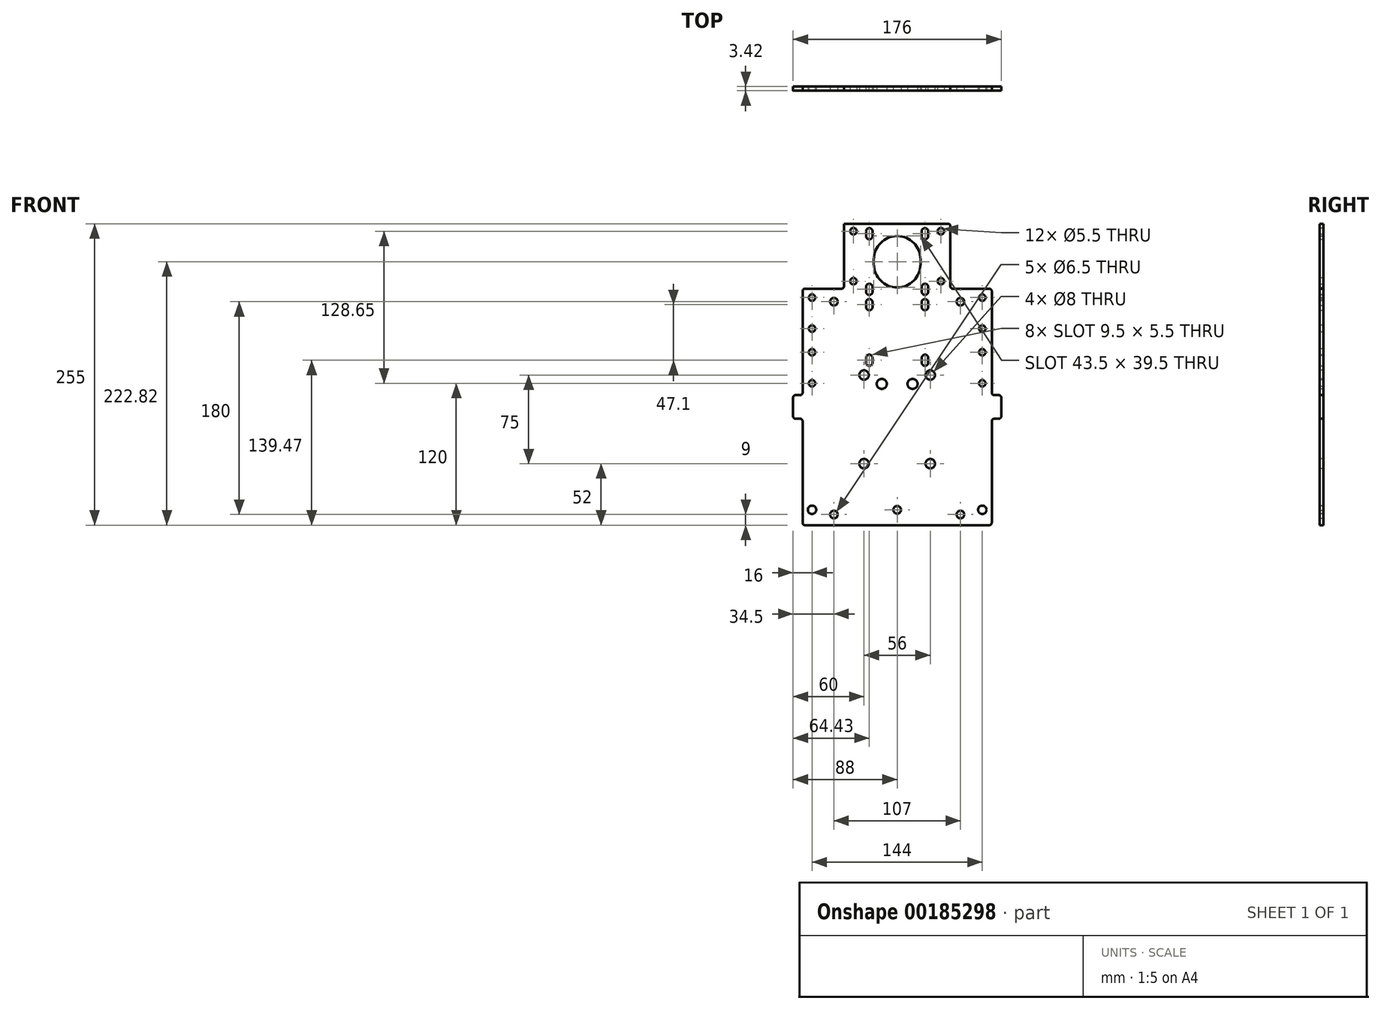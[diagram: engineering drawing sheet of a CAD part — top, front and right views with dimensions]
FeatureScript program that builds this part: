
annotation { "Feature Type Name" : "Feature", "Feature Type Description" : "" }
export const myFeature = defineFeature(function(context is Context, id is Id, definition is map)
    precondition{}
    {
        {
            var Q0;
            Q0=qCreatedBy(makeId("Front.planeOp"),FACE);
            var sketch = newSketch(context, id + "F0", { "sketchPlane" : qUnion([Q0])});
            skLineSegment(sketch, "E0", {"start": v(-80, -100) * mm, "end": v(80, -100) * mm});
            skLineSegment(sketch, "E1", {"start": v(80, -100) * mm, "end": v(80, -10) * mm});
            skLineSegment(sketch, "E2", {"start": v(80, -10) * mm, "end": v(88, -10) * mm});
            skLineSegment(sketch, "E3", {"start": v(88, -10) * mm, "end": v(88, 10) * mm});
            skLineSegment(sketch, "E4", {"start": v(88, 10) * mm, "end": v(80, 10) * mm});
            skLineSegment(sketch, "E5", {"start": v(80, 10) * mm, "end": v(80, 100) * mm});
            skLineSegment(sketch, "E6", {"start": v(80, 100) * mm, "end": v(45, 100) * mm});
            skLineSegment(sketch, "E7", {"start": v(45, 100) * mm, "end": v(45, 155) * mm});
            skLineSegment(sketch, "E8", {"start": v(45, 155) * mm, "end": v(-45, 155) * mm});
            skLineSegment(sketch, "E9", {"start": v(-45, 155) * mm, "end": v(-45, 100) * mm});
            skLineSegment(sketch, "E10", {"start": v(-45, 100) * mm, "end": v(-80, 100) * mm});
            skLineSegment(sketch, "E11", {"start": v(-80, 100) * mm, "end": v(-80, 10) * mm});
            skLineSegment(sketch, "E12", {"start": v(-80, 10) * mm, "end": v(-88, 10) * mm});
            skLineSegment(sketch, "E13", {"start": v(-88, 10) * mm, "end": v(-88, -10) * mm});
            skLineSegment(sketch, "E14", {"start": v(-88, -10) * mm, "end": v(-80, -10) * mm});
            skLineSegment(sketch, "E15", {"start": v(-80, -10) * mm, "end": v(-80, -100) * mm});
            skLineSegment(sketch, "E16", {"start": v(0, 155) * mm, "end": v(0, 0) * mm, "construction": true});
            skLineSegment(sketch, "E17", {"start": v(0, 0) * mm, "end": v(88, 0) * mm, "construction": true});
            skLineSegment(sketch, "E18", {"start": v(-19.75, 124.82) * mm, "end": v(-19.75, 120.82) * mm});
            skLineSegment(sketch, "E19", {"start": v(19.75, 124.82) * mm, "end": v(19.75, 120.82) * mm});
            skLineSegment(sketch, "E20", {"start": v(-19.75, 122.82) * mm, "end": v(19.75, 122.82) * mm, "construction": true});
            skPoint(sketch, "E21", {"position": v(0, 122.82) * mm});
            skArc(sketch, "E22", {"start": v(-19.75, 124.82) * mm, "mid": v(0, 144.57) * mm, "end": v(19.75, 124.82) * mm});
            skArc(sketch, "E23", {"start": v(-19.75, 120.82) * mm, "mid": v(0, 101.07) * mm, "end": v(19.75, 120.82) * mm});
            skLineSegment(sketch, "E24.bottom", {"start": v(-23.57, 146.57) * mm, "end": v(23.53, 146.57) * mm, "construction": true});
            skLineSegment(sketch, "E24.top", {"start": v(-23.57, 99.47) * mm, "end": v(23.53, 99.47) * mm, "construction": true});
            skLineSegment(sketch, "E24.left", {"start": v(-23.57, 146.57) * mm, "end": v(-23.57, 99.47) * mm, "construction": true});
            skLineSegment(sketch, "E24.right", {"start": v(23.53, 146.57) * mm, "end": v(23.53, 99.47) * mm, "construction": true});
            skLineSegment(sketch, "E25.bottom", {"start": v(-20.82, 148.57) * mm, "end": v(-26.32, 148.57) * mm, "construction": true});
            skLineSegment(sketch, "E25.top", {"start": v(-20.82, 144.57) * mm, "end": v(-26.32, 144.57) * mm, "construction": true});
            skLineSegment(sketch, "E25.left", {"start": v(-20.82, 148.57) * mm, "end": v(-20.82, 144.57) * mm});
            skLineSegment(sketch, "E25.right", {"start": v(-26.32, 148.57) * mm, "end": v(-26.32, 144.57) * mm});
            skPoint(sketch, "E25.middle", {"position": v(-23.57, 146.57) * mm});
            skLineSegment(sketch, "E26.bottom", {"start": v(26.28, 148.57) * mm, "end": v(20.78, 148.57) * mm, "construction": true});
            skLineSegment(sketch, "E26.top", {"start": v(26.28, 144.57) * mm, "end": v(20.78, 144.57) * mm, "construction": true});
            skLineSegment(sketch, "E26.left", {"start": v(26.28, 148.57) * mm, "end": v(26.28, 144.57) * mm});
            skLineSegment(sketch, "E26.right", {"start": v(20.78, 148.57) * mm, "end": v(20.78, 144.57) * mm});
            skPoint(sketch, "E26.middle", {"position": v(23.53, 146.57) * mm});
            skLineSegment(sketch, "E27.bottom", {"start": v(26.28, 101.47) * mm, "end": v(20.78, 101.47) * mm, "construction": true});
            skLineSegment(sketch, "E27.top", {"start": v(26.28, 97.47) * mm, "end": v(20.78, 97.47) * mm, "construction": true});
            skLineSegment(sketch, "E27.left", {"start": v(26.28, 101.47) * mm, "end": v(26.28, 97.47) * mm});
            skLineSegment(sketch, "E27.right", {"start": v(20.78, 101.47) * mm, "end": v(20.78, 97.47) * mm});
            skPoint(sketch, "E27.middle", {"position": v(23.53, 99.47) * mm});
            skLineSegment(sketch, "E28.bottom", {"start": v(-20.82, 101.47) * mm, "end": v(-26.32, 101.47) * mm, "construction": true});
            skLineSegment(sketch, "E28.top", {"start": v(-20.82, 97.47) * mm, "end": v(-26.32, 97.47) * mm, "construction": true});
            skLineSegment(sketch, "E28.left", {"start": v(-20.82, 101.47) * mm, "end": v(-20.82, 97.47) * mm});
            skLineSegment(sketch, "E28.right", {"start": v(-26.32, 101.47) * mm, "end": v(-26.32, 97.47) * mm});
            skPoint(sketch, "E28.middle", {"position": v(-23.57, 99.47) * mm});
            skLineSegment(sketch, "E29.bottom", {"start": v(-23.57, 86.57) * mm, "end": v(23.53, 86.57) * mm, "construction": true});
            skLineSegment(sketch, "E29.top", {"start": v(-23.57, 39.47) * mm, "end": v(23.53, 39.47) * mm, "construction": true});
            skLineSegment(sketch, "E29.left", {"start": v(-23.57, 86.57) * mm, "end": v(-23.57, 39.47) * mm, "construction": true});
            skLineSegment(sketch, "E29.right", {"start": v(23.53, 86.57) * mm, "end": v(23.53, 39.47) * mm, "construction": true});
            skLineSegment(sketch, "E30.bottom", {"start": v(-20.82, 88.57) * mm, "end": v(-26.32, 88.57) * mm, "construction": true});
            skLineSegment(sketch, "E30.top", {"start": v(-20.82, 84.57) * mm, "end": v(-26.32, 84.57) * mm, "construction": true});
            skLineSegment(sketch, "E30.left", {"start": v(-20.82, 88.57) * mm, "end": v(-20.82, 84.57) * mm});
            skLineSegment(sketch, "E30.right", {"start": v(-26.32, 88.57) * mm, "end": v(-26.32, 84.57) * mm});
            skPoint(sketch, "E30.middle", {"position": v(-23.57, 86.57) * mm});
            skLineSegment(sketch, "E31.bottom", {"start": v(26.28, 88.57) * mm, "end": v(20.78, 88.57) * mm, "construction": true});
            skLineSegment(sketch, "E31.top", {"start": v(26.28, 84.57) * mm, "end": v(20.78, 84.57) * mm, "construction": true});
            skLineSegment(sketch, "E31.left", {"start": v(26.28, 88.57) * mm, "end": v(26.28, 84.57) * mm});
            skLineSegment(sketch, "E31.right", {"start": v(20.78, 88.57) * mm, "end": v(20.78, 84.57) * mm});
            skPoint(sketch, "E31.middle", {"position": v(23.53, 86.57) * mm});
            skLineSegment(sketch, "E32.bottom", {"start": v(26.28, 41.47) * mm, "end": v(20.78, 41.47) * mm, "construction": true});
            skLineSegment(sketch, "E32.top", {"start": v(26.28, 37.47) * mm, "end": v(20.78, 37.47) * mm, "construction": true});
            skLineSegment(sketch, "E32.left", {"start": v(26.28, 41.47) * mm, "end": v(26.28, 37.47) * mm});
            skLineSegment(sketch, "E32.right", {"start": v(20.78, 41.47) * mm, "end": v(20.78, 37.47) * mm});
            skPoint(sketch, "E32.middle", {"position": v(23.53, 39.47) * mm});
            skLineSegment(sketch, "E33.bottom", {"start": v(-20.82, 41.47) * mm, "end": v(-26.32, 41.47) * mm, "construction": true});
            skLineSegment(sketch, "E33.top", {"start": v(-20.82, 37.47) * mm, "end": v(-26.32, 37.47) * mm, "construction": true});
            skLineSegment(sketch, "E33.left", {"start": v(-20.82, 41.47) * mm, "end": v(-20.82, 37.47) * mm});
            skLineSegment(sketch, "E33.right", {"start": v(-26.32, 41.47) * mm, "end": v(-26.32, 37.47) * mm});
            skPoint(sketch, "E33.middle", {"position": v(-23.57, 39.47) * mm});
            skArc(sketch, "E34", {"start": v(-26.32, 148.57) * mm, "mid": v(-23.57, 151.32) * mm, "end": v(-20.82, 148.57) * mm});
            skArc(sketch, "E35", {"start": v(26.28, 148.57) * mm, "mid": v(23.53, 151.32) * mm, "end": v(20.78, 148.57) * mm});
            skArc(sketch, "E36", {"start": v(20.78, 144.57) * mm, "mid": v(23.53, 141.82) * mm, "end": v(26.28, 144.57) * mm});
            skArc(sketch, "E37", {"start": v(-26.32, 144.57) * mm, "mid": v(-23.57, 141.82) * mm, "end": v(-20.82, 144.57) * mm});
            skArc(sketch, "E38", {"start": v(-20.82, 101.47) * mm, "mid": v(-23.57, 104.22) * mm, "end": v(-26.32, 101.47) * mm});
            skArc(sketch, "E39", {"start": v(-26.32, 97.47) * mm, "mid": v(-23.57, 94.72) * mm, "end": v(-20.82, 97.47) * mm});
            skArc(sketch, "E40", {"start": v(-20.82, 88.57) * mm, "mid": v(-23.57, 91.32) * mm, "end": v(-26.32, 88.57) * mm});
            skArc(sketch, "E41", {"start": v(-26.32, 84.57) * mm, "mid": v(-23.57, 81.82) * mm, "end": v(-20.82, 84.57) * mm});
            skArc(sketch, "E42", {"start": v(-20.82, 41.47) * mm, "mid": v(-23.57, 44.22) * mm, "end": v(-26.32, 41.47) * mm});
            skArc(sketch, "E43", {"start": v(-26.32, 37.47) * mm, "mid": v(-23.57, 34.72) * mm, "end": v(-20.82, 37.47) * mm});
            skArc(sketch, "E44", {"start": v(26.28, 41.47) * mm, "mid": v(23.53, 44.22) * mm, "end": v(20.78, 41.47) * mm});
            skArc(sketch, "E45", {"start": v(20.78, 37.47) * mm, "mid": v(23.53, 34.72) * mm, "end": v(26.28, 37.47) * mm});
            skArc(sketch, "E46", {"start": v(20.78, 84.57) * mm, "mid": v(23.53, 81.82) * mm, "end": v(26.28, 84.57) * mm});
            skArc(sketch, "E47", {"start": v(26.28, 88.57) * mm, "mid": v(23.53, 91.32) * mm, "end": v(20.78, 88.57) * mm});
            skArc(sketch, "E48", {"start": v(20.78, 97.47) * mm, "mid": v(23.53, 94.72) * mm, "end": v(26.28, 97.47) * mm});
            skArc(sketch, "E49", {"start": v(26.28, 101.47) * mm, "mid": v(23.53, 104.22) * mm, "end": v(20.78, 101.47) * mm});
            skSolve(sketch);
        }
        {
            var Q0;
            Q0 = qSketchRegion(id + "F0", true);
            extrude(context, id + "F1", {"entities" : qUnion([Q0]), "depth" : 3.42 * mm});
        }
        {
            var Q0;
            Q0=makeQuery(id+"F1.opExtrude","SWEPT_EDGE",EDGE,{"disambiguationData":[OSD([sQuery(id+"F0.wireOp",EDGE,"E7"),sQuery(id+"F0.wireOp",EDGE,"E8")])]});
            var Q1;
            Q1=makeQuery(id+"F1.opExtrude","SWEPT_EDGE",EDGE,{"disambiguationData":[OSD([sQuery(id+"F0.wireOp",EDGE,"E6"),sQuery(id+"F0.wireOp",EDGE,"E7")])]});
            var Q2;
            Q2=makeQuery(id+"F1.opExtrude","SWEPT_EDGE",EDGE,{"disambiguationData":[OSD([sQuery(id+"F0.wireOp",EDGE,"E5"),sQuery(id+"F0.wireOp",EDGE,"E6")])]});
            var Q3;
            Q3=makeQuery(id+"F1.opExtrude","SWEPT_EDGE",EDGE,{"disambiguationData":[OSD([sQuery(id+"F0.wireOp",EDGE,"E9"),sQuery(id+"F0.wireOp",EDGE,"E10")])]});
            var Q4;
            Q4=makeQuery(id+"F1.opExtrude","SWEPT_EDGE",EDGE,{"disambiguationData":[OSD([sQuery(id+"F0.wireOp",EDGE,"E10"),sQuery(id+"F0.wireOp",EDGE,"E11")])]});
            var Q5;
            Q5=makeQuery(id+"F1.opExtrude","SWEPT_EDGE",EDGE,{"disambiguationData":[OSD([sQuery(id+"F0.wireOp",EDGE,"E11"),sQuery(id+"F0.wireOp",EDGE,"E12")])]});
            var Q6;
            Q6=makeQuery(id+"F1.opExtrude","SWEPT_EDGE",EDGE,{"disambiguationData":[OSD([sQuery(id+"F0.wireOp",EDGE,"E12"),sQuery(id+"F0.wireOp",EDGE,"E13")])]});
            var Q7;
            Q7=makeQuery(id+"F1.opExtrude","SWEPT_EDGE",EDGE,{"disambiguationData":[OSD([sQuery(id+"F0.wireOp",EDGE,"E13"),sQuery(id+"F0.wireOp",EDGE,"E14")])]});
            var Q8;
            Q8=makeQuery(id+"F1.opExtrude","SWEPT_EDGE",EDGE,{"disambiguationData":[OSD([sQuery(id+"F0.wireOp",EDGE,"E14"),sQuery(id+"F0.wireOp",EDGE,"E15")])]});
            var Q9;
            Q9=makeQuery(id+"F1.opExtrude","SWEPT_EDGE",EDGE,{"disambiguationData":[OSD([sQuery(id+"F0.wireOp",EDGE,"E0"),sQuery(id+"F0.wireOp",EDGE,"E15")])]});
            var Q10;
            Q10=makeQuery(id+"F1.opExtrude","SWEPT_EDGE",EDGE,{"disambiguationData":[OSD([sQuery(id+"F0.wireOp",EDGE,"E0"),sQuery(id+"F0.wireOp",EDGE,"E1")])]});
            var Q11;
            Q11=makeQuery(id+"F1.opExtrude","SWEPT_EDGE",EDGE,{"disambiguationData":[OSD([sQuery(id+"F0.wireOp",EDGE,"E1"),sQuery(id+"F0.wireOp",EDGE,"E2")])]});
            var Q12;
            Q12=makeQuery(id+"F1.opExtrude","SWEPT_EDGE",EDGE,{"disambiguationData":[OSD([sQuery(id+"F0.wireOp",EDGE,"E2"),sQuery(id+"F0.wireOp",EDGE,"E3")])]});
            var Q13;
            Q13=makeQuery(id+"F1.opExtrude","SWEPT_EDGE",EDGE,{"disambiguationData":[OSD([sQuery(id+"F0.wireOp",EDGE,"E3"),sQuery(id+"F0.wireOp",EDGE,"E4")])]});
            var Q14;
            Q14=makeQuery(id+"F1.opExtrude","SWEPT_EDGE",EDGE,{"disambiguationData":[OSD([sQuery(id+"F0.wireOp",EDGE,"E4"),sQuery(id+"F0.wireOp",EDGE,"E5")])]});
            fillet(context, id + "F2", {"entities" : qUnion([Q0, Q1, Q2, Q3, Q4, Q5, Q6, Q7, Q8, Q9, Q10, Q11, Q12, Q13, Q14]), "radius" : 2 * mm, "tangentPropagation" : true, "allowEdgeOverflow" : false});
        }
        {
            var Q0;
            Q0=makeQuery(id+"F1.opExtrude","CAP_FACE",FACE,{"disambiguationData":[OSD([sQuery(id+"F0.wireOp",EDGE,"E0"),sQuery(id+"F0.wireOp",EDGE,"E1"),sQuery(id+"F0.wireOp",EDGE,"E2"),sQuery(id+"F0.wireOp",EDGE,"E3"),sQuery(id+"F0.wireOp",EDGE,"E4"),sQuery(id+"F0.wireOp",EDGE,"E5"),sQuery(id+"F0.wireOp",EDGE,"E6"),sQuery(id+"F0.wireOp",EDGE,"E7"),sQuery(id+"F0.wireOp",EDGE,"E8"),sQuery(id+"F0.wireOp",EDGE,"E9"),sQuery(id+"F0.wireOp",EDGE,"E10"),sQuery(id+"F0.wireOp",EDGE,"E11"),sQuery(id+"F0.wireOp",EDGE,"E12"),sQuery(id+"F0.wireOp",EDGE,"E13"),sQuery(id+"F0.wireOp",EDGE,"E14"),sQuery(id+"F0.wireOp",EDGE,"E15"),sQuery(id+"F0.wireOp",EDGE,"E18"),sQuery(id+"F0.wireOp",EDGE,"E19"),sQuery(id+"F0.wireOp",EDGE,"E22"),sQuery(id+"F0.wireOp",EDGE,"E23"),sQuery(id+"F0.wireOp",EDGE,"E25.left"),sQuery(id+"F0.wireOp",EDGE,"E25.right"),sQuery(id+"F0.wireOp",EDGE,"E26.left"),sQuery(id+"F0.wireOp",EDGE,"E26.right"),sQuery(id+"F0.wireOp",EDGE,"E27.left"),sQuery(id+"F0.wireOp",EDGE,"E27.right"),sQuery(id+"F0.wireOp",EDGE,"E28.left"),sQuery(id+"F0.wireOp",EDGE,"E28.right"),sQuery(id+"F0.wireOp",EDGE,"E30.left"),sQuery(id+"F0.wireOp",EDGE,"E30.right"),sQuery(id+"F0.wireOp",EDGE,"E31.left"),sQuery(id+"F0.wireOp",EDGE,"E31.right"),sQuery(id+"F0.wireOp",EDGE,"E32.left"),sQuery(id+"F0.wireOp",EDGE,"E32.right"),sQuery(id+"F0.wireOp",EDGE,"E33.left"),sQuery(id+"F0.wireOp",EDGE,"E33.right"),sQuery(id+"F0.wireOp",EDGE,"E34"),sQuery(id+"F0.wireOp",EDGE,"E35"),sQuery(id+"F0.wireOp",EDGE,"E36"),sQuery(id+"F0.wireOp",EDGE,"E37"),sQuery(id+"F0.wireOp",EDGE,"E38"),sQuery(id+"F0.wireOp",EDGE,"E39"),sQuery(id+"F0.wireOp",EDGE,"E40"),sQuery(id+"F0.wireOp",EDGE,"E41"),sQuery(id+"F0.wireOp",EDGE,"E42"),sQuery(id+"F0.wireOp",EDGE,"E43"),sQuery(id+"F0.wireOp",EDGE,"E44"),sQuery(id+"F0.wireOp",EDGE,"E45"),sQuery(id+"F0.wireOp",EDGE,"E46"),sQuery(id+"F0.wireOp",EDGE,"E47"),sQuery(id+"F0.wireOp",EDGE,"E48"),sQuery(id+"F0.wireOp",EDGE,"E49")])],"isStart":false});
            var sketch = newSketch(context, id + "F3", { "sketchPlane" : qUnion([Q0])});
            skLineSegment(sketch, "E50.bottom", {"start": v(-37, 148.65) * mm, "end": v(37, 148.65) * mm, "construction": true});
            skLineSegment(sketch, "E50.top", {"start": v(-37, 106.35) * mm, "end": v(37, 106.35) * mm, "construction": true});
            skLineSegment(sketch, "E50.left", {"start": v(-37, 148.65) * mm, "end": v(-37, 106.35) * mm, "construction": true});
            skLineSegment(sketch, "E50.right", {"start": v(37, 148.65) * mm, "end": v(37, 106.35) * mm, "construction": true});
            skLineSegment(sketch, "E51.bottom", {"start": v(-72, 92.5) * mm, "end": v(72, 92.5) * mm, "construction": true});
            skLineSegment(sketch, "E51.top", {"start": v(-72, 66.25) * mm, "end": v(72, 66.25) * mm, "construction": true});
            skLineSegment(sketch, "E51.left", {"start": v(-72, 92.5) * mm, "end": v(-72, 66.25) * mm, "construction": true});
            skLineSegment(sketch, "E51.right", {"start": v(72, 92.5) * mm, "end": v(72, 66.25) * mm, "construction": true});
            skLineSegment(sketch, "E52.bottom", {"start": v(-72, 46.25) * mm, "end": v(72, 46.25) * mm, "construction": true});
            skLineSegment(sketch, "E52.top", {"start": v(-72, 20) * mm, "end": v(72, 20) * mm, "construction": true});
            skLineSegment(sketch, "E52.left", {"start": v(-72, 46.25) * mm, "end": v(-72, 20) * mm, "construction": true});
            skLineSegment(sketch, "E52.right", {"start": v(72, 46.25) * mm, "end": v(72, 20) * mm, "construction": true});
            skLineSegment(sketch, "E53.bottom", {"start": v(-28, 27) * mm, "end": v(28, 27) * mm, "construction": true});
            skLineSegment(sketch, "E53.top", {"start": v(-28, -48) * mm, "end": v(28, -48) * mm, "construction": true});
            skLineSegment(sketch, "E53.left", {"start": v(-28, 27) * mm, "end": v(-28, -48) * mm, "construction": true});
            skLineSegment(sketch, "E53.right", {"start": v(28, 27) * mm, "end": v(28, -48) * mm, "construction": true});
            skLineSegment(sketch, "E54", {"start": v(-72, -87) * mm, "end": v(0, -87) * mm, "construction": true});
            skLineSegment(sketch, "E55", {"start": v(0, -87) * mm, "end": v(72, -87) * mm, "construction": true});
            skLineSegment(sketch, "E56", {"start": v(72, -87) * mm, "end": v(53.5, -91) * mm, "construction": true});
            skLineSegment(sketch, "E57", {"start": v(53.5, -91) * mm, "end": v(-53.5, -91) * mm, "construction": true});
            skLineSegment(sketch, "E58", {"start": v(-53.5, -91) * mm, "end": v(-72, -87) * mm, "construction": true});
            skLineSegment(sketch, "E59", {"start": v(-28, 19.5) * mm, "end": v(-13, 19.5) * mm, "construction": true});
            skLineSegment(sketch, "E60", {"start": v(-13, 19.5) * mm, "end": v(13, 19.5) * mm, "construction": true});
            skLineSegment(sketch, "E61", {"start": v(13, 19.5) * mm, "end": v(28, 19.5) * mm, "construction": true});
            skLineSegment(sketch, "E62", {"start": v(0, 19.5) * mm, "end": v(0, 0) * mm, "construction": true});
            skLineSegment(sketch, "E63", {"start": v(-53.5, -91) * mm, "end": v(-53.5, 89) * mm, "construction": true});
            skLineSegment(sketch, "E64", {"start": v(-53.5, 89) * mm, "end": v(53.5, 89) * mm, "construction": true});
            skLineSegment(sketch, "E65", {"start": v(53.5, 89) * mm, "end": v(53.5, -91) * mm, "construction": true});
            skSolve(sketch);
        }
        {
            var Q0;
            Q0=sQuery(id+"F3.wireOp",VERTEX,"E53.left.start");
            var Q1;
            Q1=sQuery(id+"F3.wireOp",VERTEX,"E53.right.start");
            var Q2;
            Q2=sQuery(id+"F3.wireOp",VERTEX,"E53.top.end");
            var Q3;
            Q3=sQuery(id+"F3.wireOp",VERTEX,"E53.top.start");
            var Q4;
            Q4=makeQuery(id+"F1.opExtrude","SWEPT_BODY",BODY,{"disambiguationData":[OSD([sQuery(id+"F0.wireOp",EDGE,"E0"),sQuery(id+"F0.wireOp",EDGE,"E1"),sQuery(id+"F0.wireOp",EDGE,"E2"),sQuery(id+"F0.wireOp",EDGE,"E3"),sQuery(id+"F0.wireOp",EDGE,"E4"),sQuery(id+"F0.wireOp",EDGE,"E5"),sQuery(id+"F0.wireOp",EDGE,"E6"),sQuery(id+"F0.wireOp",EDGE,"E7"),sQuery(id+"F0.wireOp",EDGE,"E8"),sQuery(id+"F0.wireOp",EDGE,"E9"),sQuery(id+"F0.wireOp",EDGE,"E10"),sQuery(id+"F0.wireOp",EDGE,"E11"),sQuery(id+"F0.wireOp",EDGE,"E12"),sQuery(id+"F0.wireOp",EDGE,"E13"),sQuery(id+"F0.wireOp",EDGE,"E14"),sQuery(id+"F0.wireOp",EDGE,"E15"),sQuery(id+"F0.wireOp",EDGE,"E18"),sQuery(id+"F0.wireOp",EDGE,"E19"),sQuery(id+"F0.wireOp",EDGE,"E22"),sQuery(id+"F0.wireOp",EDGE,"E23"),sQuery(id+"F0.wireOp",EDGE,"E25.left"),sQuery(id+"F0.wireOp",EDGE,"E25.right"),sQuery(id+"F0.wireOp",EDGE,"E26.left"),sQuery(id+"F0.wireOp",EDGE,"E26.right"),sQuery(id+"F0.wireOp",EDGE,"E27.left"),sQuery(id+"F0.wireOp",EDGE,"E27.right"),sQuery(id+"F0.wireOp",EDGE,"E28.left"),sQuery(id+"F0.wireOp",EDGE,"E28.right"),sQuery(id+"F0.wireOp",EDGE,"E30.left"),sQuery(id+"F0.wireOp",EDGE,"E30.right"),sQuery(id+"F0.wireOp",EDGE,"E31.left"),sQuery(id+"F0.wireOp",EDGE,"E31.right"),sQuery(id+"F0.wireOp",EDGE,"E32.left"),sQuery(id+"F0.wireOp",EDGE,"E32.right"),sQuery(id+"F0.wireOp",EDGE,"E33.left"),sQuery(id+"F0.wireOp",EDGE,"E33.right"),sQuery(id+"F0.wireOp",EDGE,"E34"),sQuery(id+"F0.wireOp",EDGE,"E35"),sQuery(id+"F0.wireOp",EDGE,"E36"),sQuery(id+"F0.wireOp",EDGE,"E37"),sQuery(id+"F0.wireOp",EDGE,"E38"),sQuery(id+"F0.wireOp",EDGE,"E39"),sQuery(id+"F0.wireOp",EDGE,"E40"),sQuery(id+"F0.wireOp",EDGE,"E41"),sQuery(id+"F0.wireOp",EDGE,"E42"),sQuery(id+"F0.wireOp",EDGE,"E43"),sQuery(id+"F0.wireOp",EDGE,"E44"),sQuery(id+"F0.wireOp",EDGE,"E45"),sQuery(id+"F0.wireOp",EDGE,"E46"),sQuery(id+"F0.wireOp",EDGE,"E47"),sQuery(id+"F0.wireOp",EDGE,"E48"),sQuery(id+"F0.wireOp",EDGE,"E49")])]});
            hole(context, id + "F4", {"style" : HoleStyle.SIMPLE, "endStyle" : HoleEndStyle.THROUGH, "holeDiameter" : 8 * mm, "locations" : qUnion([Q0, Q1, Q2, Q3]), "scope" : qUnion([Q4]), "isTappedThrough" : true});
        }
        {
            var Q0;
            Q0=sQuery(id+"F3.wireOp",VERTEX,"E60.start");
            var Q1;
            Q1=sQuery(id+"F3.wireOp",VERTEX,"E61.start");
            var Q2;
            Q2=makeQuery(id+"F1.opExtrude","SWEPT_BODY",BODY,{"disambiguationData":[OSD([sQuery(id+"F0.wireOp",EDGE,"E0"),sQuery(id+"F0.wireOp",EDGE,"E1"),sQuery(id+"F0.wireOp",EDGE,"E2"),sQuery(id+"F0.wireOp",EDGE,"E3"),sQuery(id+"F0.wireOp",EDGE,"E4"),sQuery(id+"F0.wireOp",EDGE,"E5"),sQuery(id+"F0.wireOp",EDGE,"E6"),sQuery(id+"F0.wireOp",EDGE,"E7"),sQuery(id+"F0.wireOp",EDGE,"E8"),sQuery(id+"F0.wireOp",EDGE,"E9"),sQuery(id+"F0.wireOp",EDGE,"E10"),sQuery(id+"F0.wireOp",EDGE,"E11"),sQuery(id+"F0.wireOp",EDGE,"E12"),sQuery(id+"F0.wireOp",EDGE,"E13"),sQuery(id+"F0.wireOp",EDGE,"E14"),sQuery(id+"F0.wireOp",EDGE,"E15"),sQuery(id+"F0.wireOp",EDGE,"E18"),sQuery(id+"F0.wireOp",EDGE,"E19"),sQuery(id+"F0.wireOp",EDGE,"E22"),sQuery(id+"F0.wireOp",EDGE,"E23"),sQuery(id+"F0.wireOp",EDGE,"E25.left"),sQuery(id+"F0.wireOp",EDGE,"E25.right"),sQuery(id+"F0.wireOp",EDGE,"E26.left"),sQuery(id+"F0.wireOp",EDGE,"E26.right"),sQuery(id+"F0.wireOp",EDGE,"E27.left"),sQuery(id+"F0.wireOp",EDGE,"E27.right"),sQuery(id+"F0.wireOp",EDGE,"E28.left"),sQuery(id+"F0.wireOp",EDGE,"E28.right"),sQuery(id+"F0.wireOp",EDGE,"E30.left"),sQuery(id+"F0.wireOp",EDGE,"E30.right"),sQuery(id+"F0.wireOp",EDGE,"E31.left"),sQuery(id+"F0.wireOp",EDGE,"E31.right"),sQuery(id+"F0.wireOp",EDGE,"E32.left"),sQuery(id+"F0.wireOp",EDGE,"E32.right"),sQuery(id+"F0.wireOp",EDGE,"E33.left"),sQuery(id+"F0.wireOp",EDGE,"E33.right"),sQuery(id+"F0.wireOp",EDGE,"E34"),sQuery(id+"F0.wireOp",EDGE,"E35"),sQuery(id+"F0.wireOp",EDGE,"E36"),sQuery(id+"F0.wireOp",EDGE,"E37"),sQuery(id+"F0.wireOp",EDGE,"E38"),sQuery(id+"F0.wireOp",EDGE,"E39"),sQuery(id+"F0.wireOp",EDGE,"E40"),sQuery(id+"F0.wireOp",EDGE,"E41"),sQuery(id+"F0.wireOp",EDGE,"E42"),sQuery(id+"F0.wireOp",EDGE,"E43"),sQuery(id+"F0.wireOp",EDGE,"E44"),sQuery(id+"F0.wireOp",EDGE,"E45"),sQuery(id+"F0.wireOp",EDGE,"E46"),sQuery(id+"F0.wireOp",EDGE,"E47"),sQuery(id+"F0.wireOp",EDGE,"E48"),sQuery(id+"F0.wireOp",EDGE,"E49")])]});
            hole(context, id + "F5", {"style" : HoleStyle.SIMPLE, "endStyle" : HoleEndStyle.THROUGH, "holeDiameter" : 8.5 * mm, "locations" : qUnion([Q0, Q1]), "scope" : qUnion([Q2]), "isTappedThrough" : true});
        }
        {
            var Q0;
            Q0=sQuery(id+"F3.wireOp",VERTEX,"E64.start");
            var Q1;
            Q1=sQuery(id+"F3.wireOp",VERTEX,"E65.start");
            var Q2;
            Q2=sQuery(id+"F3.wireOp",VERTEX,"E57.end");
            var Q3;
            Q3=sQuery(id+"F3.wireOp",VERTEX,"E65.end");
            var Q4;
            Q4=sQuery(id+"F3.wireOp",VERTEX,"E55.start");
            var Q5;
            Q5=makeQuery(id+"F1.opExtrude","SWEPT_BODY",BODY,{"disambiguationData":[OSD([sQuery(id+"F0.wireOp",EDGE,"E0"),sQuery(id+"F0.wireOp",EDGE,"E1"),sQuery(id+"F0.wireOp",EDGE,"E2"),sQuery(id+"F0.wireOp",EDGE,"E3"),sQuery(id+"F0.wireOp",EDGE,"E4"),sQuery(id+"F0.wireOp",EDGE,"E5"),sQuery(id+"F0.wireOp",EDGE,"E6"),sQuery(id+"F0.wireOp",EDGE,"E7"),sQuery(id+"F0.wireOp",EDGE,"E8"),sQuery(id+"F0.wireOp",EDGE,"E9"),sQuery(id+"F0.wireOp",EDGE,"E10"),sQuery(id+"F0.wireOp",EDGE,"E11"),sQuery(id+"F0.wireOp",EDGE,"E12"),sQuery(id+"F0.wireOp",EDGE,"E13"),sQuery(id+"F0.wireOp",EDGE,"E14"),sQuery(id+"F0.wireOp",EDGE,"E15"),sQuery(id+"F0.wireOp",EDGE,"E18"),sQuery(id+"F0.wireOp",EDGE,"E19"),sQuery(id+"F0.wireOp",EDGE,"E22"),sQuery(id+"F0.wireOp",EDGE,"E23"),sQuery(id+"F0.wireOp",EDGE,"E25.left"),sQuery(id+"F0.wireOp",EDGE,"E25.right"),sQuery(id+"F0.wireOp",EDGE,"E26.left"),sQuery(id+"F0.wireOp",EDGE,"E26.right"),sQuery(id+"F0.wireOp",EDGE,"E27.left"),sQuery(id+"F0.wireOp",EDGE,"E27.right"),sQuery(id+"F0.wireOp",EDGE,"E28.left"),sQuery(id+"F0.wireOp",EDGE,"E28.right"),sQuery(id+"F0.wireOp",EDGE,"E30.left"),sQuery(id+"F0.wireOp",EDGE,"E30.right"),sQuery(id+"F0.wireOp",EDGE,"E31.left"),sQuery(id+"F0.wireOp",EDGE,"E31.right"),sQuery(id+"F0.wireOp",EDGE,"E32.left"),sQuery(id+"F0.wireOp",EDGE,"E32.right"),sQuery(id+"F0.wireOp",EDGE,"E33.left"),sQuery(id+"F0.wireOp",EDGE,"E33.right"),sQuery(id+"F0.wireOp",EDGE,"E34"),sQuery(id+"F0.wireOp",EDGE,"E35"),sQuery(id+"F0.wireOp",EDGE,"E36"),sQuery(id+"F0.wireOp",EDGE,"E37"),sQuery(id+"F0.wireOp",EDGE,"E38"),sQuery(id+"F0.wireOp",EDGE,"E39"),sQuery(id+"F0.wireOp",EDGE,"E40"),sQuery(id+"F0.wireOp",EDGE,"E41"),sQuery(id+"F0.wireOp",EDGE,"E42"),sQuery(id+"F0.wireOp",EDGE,"E43"),sQuery(id+"F0.wireOp",EDGE,"E44"),sQuery(id+"F0.wireOp",EDGE,"E45"),sQuery(id+"F0.wireOp",EDGE,"E46"),sQuery(id+"F0.wireOp",EDGE,"E47"),sQuery(id+"F0.wireOp",EDGE,"E48"),sQuery(id+"F0.wireOp",EDGE,"E49")])]});
            hole(context, id + "F6", {"style" : HoleStyle.SIMPLE, "endStyle" : HoleEndStyle.THROUGH, "holeDiameter" : 6.5 * mm, "locations" : qUnion([Q0, Q1, Q2, Q3, Q4]), "scope" : qUnion([Q5]), "isTappedThrough" : true});
        }
        {
            var Q0;
            Q0=sQuery(id+"F3.wireOp",VERTEX,"E54.start");
            var Q1;
            Q1=sQuery(id+"F3.wireOp",VERTEX,"E56.start");
            var Q2;
            Q2=makeQuery(id+"F1.opExtrude","SWEPT_BODY",BODY,{"disambiguationData":[OSD([sQuery(id+"F0.wireOp",EDGE,"E0"),sQuery(id+"F0.wireOp",EDGE,"E1"),sQuery(id+"F0.wireOp",EDGE,"E2"),sQuery(id+"F0.wireOp",EDGE,"E3"),sQuery(id+"F0.wireOp",EDGE,"E4"),sQuery(id+"F0.wireOp",EDGE,"E5"),sQuery(id+"F0.wireOp",EDGE,"E6"),sQuery(id+"F0.wireOp",EDGE,"E7"),sQuery(id+"F0.wireOp",EDGE,"E8"),sQuery(id+"F0.wireOp",EDGE,"E9"),sQuery(id+"F0.wireOp",EDGE,"E10"),sQuery(id+"F0.wireOp",EDGE,"E11"),sQuery(id+"F0.wireOp",EDGE,"E12"),sQuery(id+"F0.wireOp",EDGE,"E13"),sQuery(id+"F0.wireOp",EDGE,"E14"),sQuery(id+"F0.wireOp",EDGE,"E15"),sQuery(id+"F0.wireOp",EDGE,"E18"),sQuery(id+"F0.wireOp",EDGE,"E19"),sQuery(id+"F0.wireOp",EDGE,"E22"),sQuery(id+"F0.wireOp",EDGE,"E23"),sQuery(id+"F0.wireOp",EDGE,"E25.left"),sQuery(id+"F0.wireOp",EDGE,"E25.right"),sQuery(id+"F0.wireOp",EDGE,"E26.left"),sQuery(id+"F0.wireOp",EDGE,"E26.right"),sQuery(id+"F0.wireOp",EDGE,"E27.left"),sQuery(id+"F0.wireOp",EDGE,"E27.right"),sQuery(id+"F0.wireOp",EDGE,"E28.left"),sQuery(id+"F0.wireOp",EDGE,"E28.right"),sQuery(id+"F0.wireOp",EDGE,"E30.left"),sQuery(id+"F0.wireOp",EDGE,"E30.right"),sQuery(id+"F0.wireOp",EDGE,"E31.left"),sQuery(id+"F0.wireOp",EDGE,"E31.right"),sQuery(id+"F0.wireOp",EDGE,"E32.left"),sQuery(id+"F0.wireOp",EDGE,"E32.right"),sQuery(id+"F0.wireOp",EDGE,"E33.left"),sQuery(id+"F0.wireOp",EDGE,"E33.right"),sQuery(id+"F0.wireOp",EDGE,"E34"),sQuery(id+"F0.wireOp",EDGE,"E35"),sQuery(id+"F0.wireOp",EDGE,"E36"),sQuery(id+"F0.wireOp",EDGE,"E37"),sQuery(id+"F0.wireOp",EDGE,"E38"),sQuery(id+"F0.wireOp",EDGE,"E39"),sQuery(id+"F0.wireOp",EDGE,"E40"),sQuery(id+"F0.wireOp",EDGE,"E41"),sQuery(id+"F0.wireOp",EDGE,"E42"),sQuery(id+"F0.wireOp",EDGE,"E43"),sQuery(id+"F0.wireOp",EDGE,"E44"),sQuery(id+"F0.wireOp",EDGE,"E45"),sQuery(id+"F0.wireOp",EDGE,"E46"),sQuery(id+"F0.wireOp",EDGE,"E47"),sQuery(id+"F0.wireOp",EDGE,"E48"),sQuery(id+"F0.wireOp",EDGE,"E49")])]});
            hole(context, id + "F7", {"style" : HoleStyle.SIMPLE, "endStyle" : HoleEndStyle.THROUGH, "holeDiameter" : 7.14 * mm, "locations" : qUnion([Q0, Q1]), "scope" : qUnion([Q2]), "isTappedThrough" : true});
        }
        {
            var Q0;
            Q0=sQuery(id+"F3.wireOp",VERTEX,"E50.bottom.start");
            var Q1;
            Q1=sQuery(id+"F3.wireOp",VERTEX,"E50.bottom.end");
            var Q2;
            Q2=sQuery(id+"F3.wireOp",VERTEX,"E50.right.end");
            var Q3;
            Q3=sQuery(id+"F3.wireOp",VERTEX,"E50.left.end");
            var Q4;
            Q4=sQuery(id+"F3.wireOp",VERTEX,"E51.left.start");
            var Q5;
            Q5=sQuery(id+"F3.wireOp",VERTEX,"E51.left.end");
            var Q6;
            Q6=sQuery(id+"F3.wireOp",VERTEX,"E52.top.start");
            var Q7;
            Q7=sQuery(id+"F3.wireOp",VERTEX,"E52.bottom.start");
            var Q8;
            Q8=sQuery(id+"F3.wireOp",VERTEX,"E52.bottom.end");
            var Q9;
            Q9=sQuery(id+"F3.wireOp",VERTEX,"E52.right.end");
            var Q10;
            Q10=sQuery(id+"F3.wireOp",VERTEX,"E51.right.end");
            var Q11;
            Q11=sQuery(id+"F3.wireOp",VERTEX,"E51.right.start");
            var Q12;
            Q12=makeQuery(id+"F1.opExtrude","SWEPT_BODY",BODY,{"disambiguationData":[OSD([sQuery(id+"F0.wireOp",EDGE,"E0"),sQuery(id+"F0.wireOp",EDGE,"E1"),sQuery(id+"F0.wireOp",EDGE,"E2"),sQuery(id+"F0.wireOp",EDGE,"E3"),sQuery(id+"F0.wireOp",EDGE,"E4"),sQuery(id+"F0.wireOp",EDGE,"E5"),sQuery(id+"F0.wireOp",EDGE,"E6"),sQuery(id+"F0.wireOp",EDGE,"E7"),sQuery(id+"F0.wireOp",EDGE,"E8"),sQuery(id+"F0.wireOp",EDGE,"E9"),sQuery(id+"F0.wireOp",EDGE,"E10"),sQuery(id+"F0.wireOp",EDGE,"E11"),sQuery(id+"F0.wireOp",EDGE,"E12"),sQuery(id+"F0.wireOp",EDGE,"E13"),sQuery(id+"F0.wireOp",EDGE,"E14"),sQuery(id+"F0.wireOp",EDGE,"E15"),sQuery(id+"F0.wireOp",EDGE,"E18"),sQuery(id+"F0.wireOp",EDGE,"E19"),sQuery(id+"F0.wireOp",EDGE,"E22"),sQuery(id+"F0.wireOp",EDGE,"E23"),sQuery(id+"F0.wireOp",EDGE,"E25.left"),sQuery(id+"F0.wireOp",EDGE,"E25.right"),sQuery(id+"F0.wireOp",EDGE,"E26.left"),sQuery(id+"F0.wireOp",EDGE,"E26.right"),sQuery(id+"F0.wireOp",EDGE,"E27.left"),sQuery(id+"F0.wireOp",EDGE,"E27.right"),sQuery(id+"F0.wireOp",EDGE,"E28.left"),sQuery(id+"F0.wireOp",EDGE,"E28.right"),sQuery(id+"F0.wireOp",EDGE,"E30.left"),sQuery(id+"F0.wireOp",EDGE,"E30.right"),sQuery(id+"F0.wireOp",EDGE,"E31.left"),sQuery(id+"F0.wireOp",EDGE,"E31.right"),sQuery(id+"F0.wireOp",EDGE,"E32.left"),sQuery(id+"F0.wireOp",EDGE,"E32.right"),sQuery(id+"F0.wireOp",EDGE,"E33.left"),sQuery(id+"F0.wireOp",EDGE,"E33.right"),sQuery(id+"F0.wireOp",EDGE,"E34"),sQuery(id+"F0.wireOp",EDGE,"E35"),sQuery(id+"F0.wireOp",EDGE,"E36"),sQuery(id+"F0.wireOp",EDGE,"E37"),sQuery(id+"F0.wireOp",EDGE,"E38"),sQuery(id+"F0.wireOp",EDGE,"E39"),sQuery(id+"F0.wireOp",EDGE,"E40"),sQuery(id+"F0.wireOp",EDGE,"E41"),sQuery(id+"F0.wireOp",EDGE,"E42"),sQuery(id+"F0.wireOp",EDGE,"E43"),sQuery(id+"F0.wireOp",EDGE,"E44"),sQuery(id+"F0.wireOp",EDGE,"E45"),sQuery(id+"F0.wireOp",EDGE,"E46"),sQuery(id+"F0.wireOp",EDGE,"E47"),sQuery(id+"F0.wireOp",EDGE,"E48"),sQuery(id+"F0.wireOp",EDGE,"E49")])]});
            hole(context, id + "F8", {"style" : HoleStyle.SIMPLE, "endStyle" : HoleEndStyle.THROUGH, "holeDiameter" : 5.5 * mm, "locations" : qUnion([Q0, Q1, Q2, Q3, Q4, Q5, Q6, Q7, Q8, Q9, Q10, Q11]), "scope" : qUnion([Q12]), "isTappedThrough" : true});
        }
    });
